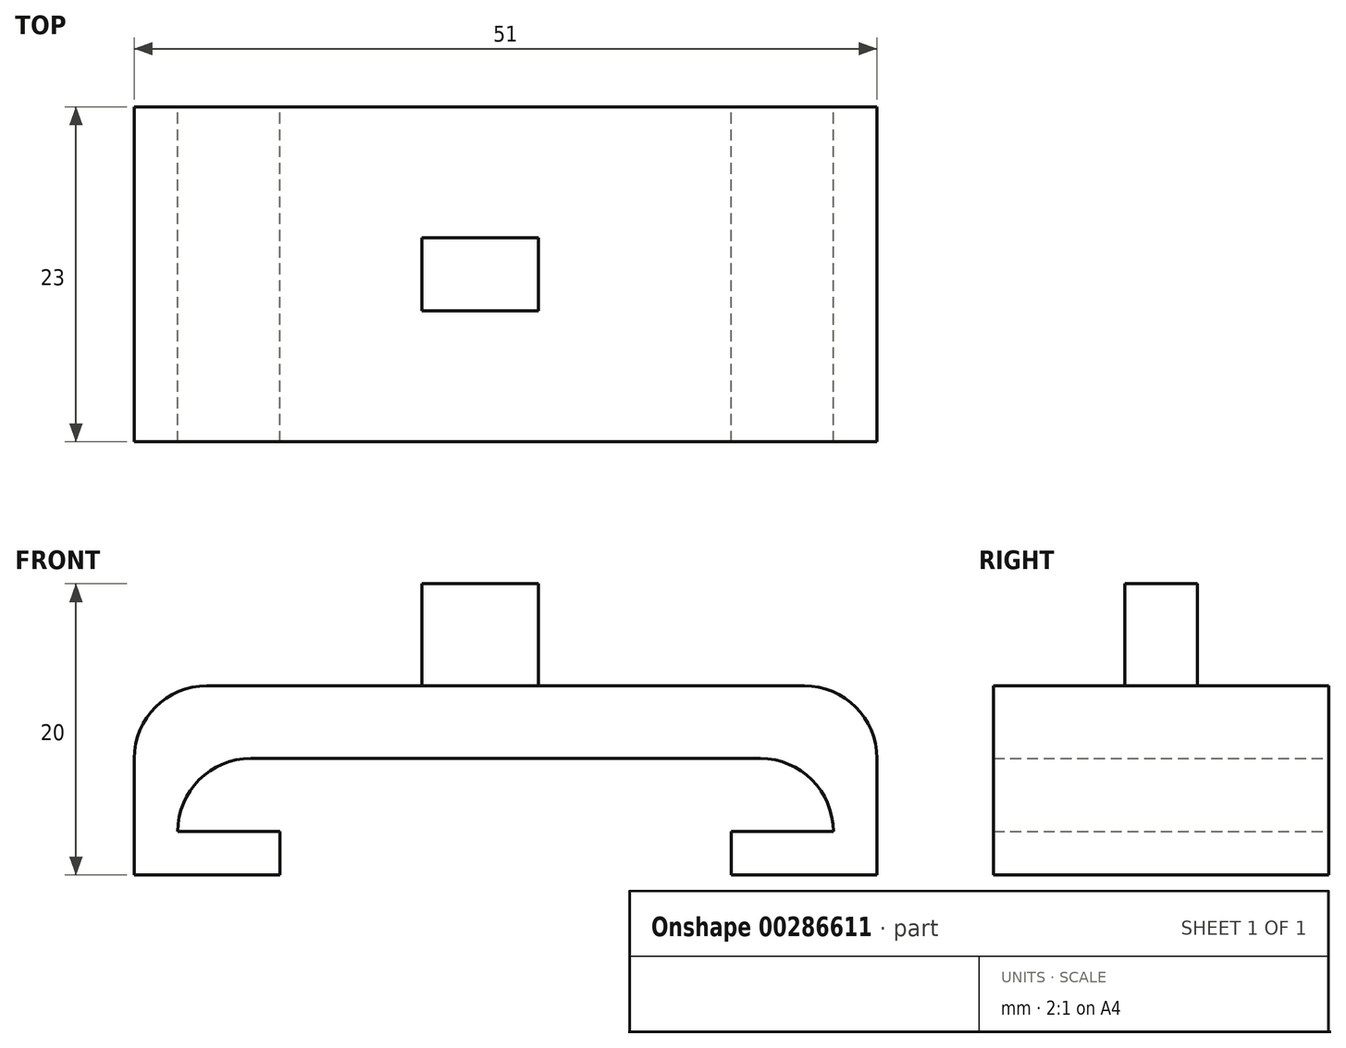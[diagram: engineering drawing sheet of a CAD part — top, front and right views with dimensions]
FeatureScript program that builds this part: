
annotation { "Feature Type Name" : "Feature", "Feature Type Description" : "" }
export const myFeature = defineFeature(function(context is Context, id is Id, definition is map)
    precondition{}
    {
        {
            var Q0;
            Q0=qCreatedBy(makeId("Front.planeOp"),FACE);
            var sketch = newSketch(context, id + "F0", { "sketchPlane" : qUnion([Q0])});
            skLineSegment(sketch, "E0", {"start": v(-15.75, 0) * mm, "end": v(19.25, 0) * mm});
            skLineSegment(sketch, "E1", {"start": v(-20.75, -5) * mm, "end": v(-20.75, -5) * mm});
            skLineSegment(sketch, "E2", {"start": v(-20.75, -5) * mm, "end": v(-13.75, -5) * mm});
            skLineSegment(sketch, "E3", {"start": v(-13.75, -5) * mm, "end": v(-13.75, -8) * mm});
            skLineSegment(sketch, "E4", {"start": v(-13.75, -8) * mm, "end": v(-23.75, -8) * mm});
            skLineSegment(sketch, "E5", {"start": v(-23.75, -8) * mm, "end": v(-23.75, 5) * mm});
            skLineSegment(sketch, "E6", {"start": v(-23.75, 5) * mm, "end": v(27.25, 5) * mm});
            skLineSegment(sketch, "E7", {"start": v(27.25, 5) * mm, "end": v(27.25, -8) * mm});
            skLineSegment(sketch, "E8", {"start": v(27.25, -8) * mm, "end": v(17.25, -8) * mm});
            skLineSegment(sketch, "E9", {"start": v(17.25, -8) * mm, "end": v(17.25, -5) * mm});
            skLineSegment(sketch, "E10", {"start": v(17.25, -5) * mm, "end": v(24.25, -5) * mm});
            skLineSegment(sketch, "E11", {"start": v(24.25, -5) * mm, "end": v(24.25, -5) * mm});
            skPoint(sketch, "E12.visualSharp", {"position": v(-20.75, 0) * mm});
            skArc(sketch, "E12.filletArc", {"start": v(-15.75, 0) * mm, "mid": v(-19.29, -1.46) * mm, "end": v(-20.75, -5) * mm});
            skPoint(sketch, "E13.visualSharp", {"position": v(24.25, 0) * mm});
            skArc(sketch, "E13.filletArc", {"start": v(24.25, -5) * mm, "mid": v(22.78, -1.46) * mm, "end": v(19.25, 0) * mm});
            skSolve(sketch);
        }
        {
            var Q0;
            Q0=makeQuery(id+"F0.imprint","IMPRINT",FACE,{"disambiguationData":[TD([[makeQuery(id+"F0.imprint","IMPRINT",EDGE,{"derivedFrom":sQuery(id+"F0.wireOp",EDGE,"E0")}),1.0]])]});
            extrude(context, id + "F1", {"entities" : qUnion([Q0]), "depth" : 23 * mm});
        }
        {
            var Q0;
            Q0=makeQuery(id+"F1.opExtrude","SWEPT_EDGE",EDGE,{"disambiguationData":[OSD([sQuery(id+"F0.wireOp",EDGE,"E6"),sQuery(id+"F0.wireOp",EDGE,"E7")])]});
            var Q1;
            Q1=makeQuery(id+"F1.opExtrude","SWEPT_EDGE",EDGE,{"disambiguationData":[OSD([sQuery(id+"F0.wireOp",EDGE,"E5"),sQuery(id+"F0.wireOp",EDGE,"E6")])]});
            fillet(context, id + "F2", {"entities" : qUnion([Q0, Q1]), "radius" : 5 * mm, "tangentPropagation" : true, "allowEdgeOverflow" : false});
        }
        {
            var Q0;
            Q0=makeQuery(id+"F1.opExtrude","SWEPT_FACE",FACE,{"disambiguationData":[OSD([sQuery(id+"F0.wireOp",EDGE,"E6")])]});
            var sketch = newSketch(context, id + "F3", { "sketchPlane" : qUnion([Q0])});
            skLineSegment(sketch, "E14.bottom", {"start": v(-4, -9) * mm, "end": v(4, -9) * mm});
            skLineSegment(sketch, "E14.top", {"start": v(-4, -14) * mm, "end": v(4, -14) * mm});
            skLineSegment(sketch, "E14.left", {"start": v(-4, -9) * mm, "end": v(-4, -14) * mm});
            skLineSegment(sketch, "E14.right", {"start": v(4, -9) * mm, "end": v(4, -14) * mm});
            skPoint(sketch, "E14.middle", {"position": v(0, -11.5) * mm});
            skPoint(sketch, "E14.middle.positionSnap0", {"position": v(-18.75, -11.5) * mm});
            skPoint(sketch, "E14.centerSnap0", {"position": v(-18.75, -11.5) * mm});
            skSolve(sketch);
        }
        {
            var Q0;
            Q0=makeQuery(id+"F3.imprint","IMPRINT",FACE,{"disambiguationData":[TD([[makeQuery(id+"F3.imprint","IMPRINT",EDGE,{"derivedFrom":sQuery(id+"F3.wireOp",EDGE,"E14.bottom")}),-1.0]])]});
            extrude(context, id + "F4", {"entities" : qUnion([Q0]), "operationType" : NewBodyOperationType.ADD, "depth" : 7 * mm});
        }
    });
